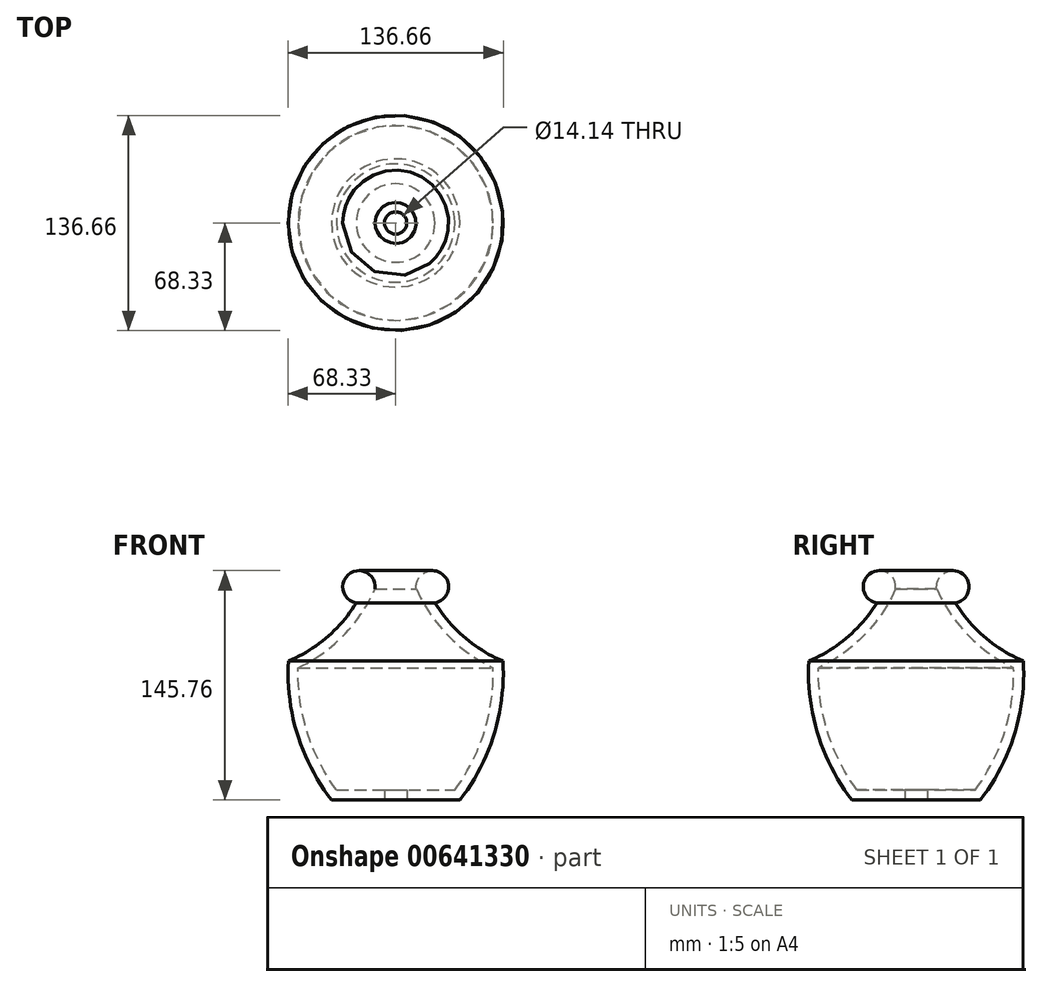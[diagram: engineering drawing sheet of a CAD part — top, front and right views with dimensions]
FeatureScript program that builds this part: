
annotation { "Feature Type Name" : "Feature", "Feature Type Description" : "" }
export const myFeature = defineFeature(function(context is Context, id is Id, definition is map)
    precondition{}
    {
        {
            var Q0;
            Q0=qCreatedBy(makeId("Front.planeOp"),FACE);
            var sketch = newSketch(context, id + "F0", { "sketchPlane" : qUnion([Q0])});
            skLineSegment(sketch, "E0", {"start": v(-7.07, -59.37) * mm, "end": v(-37.57, -59.37) * mm});
            skArc(sketch, "E1", {"start": v(-61.94, 18.37) * mm, "mid": v(-56.2, -22.53) * mm, "end": v(-37.57, -59.37) * mm});
            skArc(sketch, "E2", {"start": v(-61.94, 18.37) * mm, "mid": v(-33.02, 39) * mm, "end": v(-13.1, 68.43) * mm});
            skPoint(sketch, "E3.orphan", {"position": v(-75.13, -59.37) * mm});
            skArc(sketch, "E4.0", {"start": v(-68.13, 22.55) * mm, "mid": v(-43.66, 37.72) * mm, "end": v(-24.94, 59.59) * mm});
            skArc(sketch, "E5.0", {"start": v(-68.13, 22.55) * mm, "mid": v(-62.38, -24.05) * mm, "end": v(-40.73, -65.72) * mm});
            skLineSegment(sketch, "E6.0", {"start": v(-7.07, -65.72) * mm, "end": v(-40.73, -65.72) * mm});
            skPoint(sketch, "E7.center.orphan", {"position": v(0, 69.37) * mm});
            skArc(sketch, "E8", {"start": v(-13.1, 68.43) * mm, "mid": v(-29.48, 78) * mm, "end": v(-24.94, 59.59) * mm});
            skLineSegment(sketch, "E9", {"start": v(-7.07, -59.37) * mm, "end": v(-7.07, -65.72) * mm});
            skPoint(sketch, "E10.start.orphan", {"position": v(0, -59.37) * mm});
            skSolve(sketch);
        }
        {
            var Q0;
            Q0=qCreatedBy(makeId("Front.planeOp"),FACE);
            var sketch = newSketch(context, id + "F1", { "sketchPlane" : qUnion([Q0])});
            skLineSegment(sketch, "E11", {"start": v(0, 0) * mm, "end": v(0, 129.7) * mm});
            skSolve(sketch);
        }
        {
            var Q0;
            Q0 = qSketchRegion(id + "F0", true);
            var Q1;
            Q1=sQuery(id+"F1.wireOp",EDGE,"E11");
            revolve(context, id + "F2", {"entities" : qUnion([Q0]), "axis" : qUnion([Q1]), "revolveType" : RevolveType.FULL});
        }
    });
